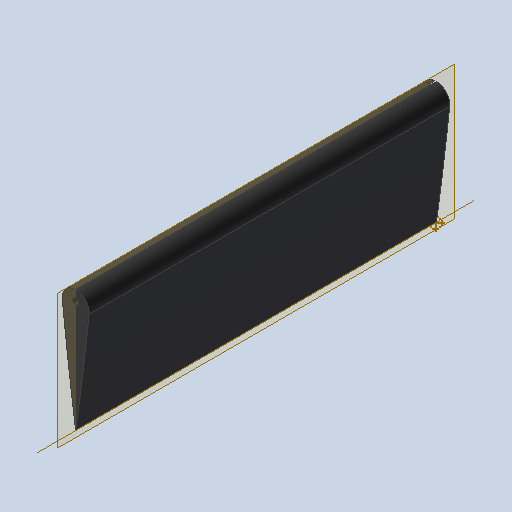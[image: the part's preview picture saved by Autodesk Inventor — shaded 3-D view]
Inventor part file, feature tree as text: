
AUTODESK INVENTOR PART (.ipt)
format: ipt  version: 2025.2 (Build 292293000, 293)  size: 150,016 bytes
history: native  units: in
note: dims shown in document units (in); Inventor stores cm internally (conversion verified against a paired STEP export)
features: other x5, sketch x1, plane x1
ambient origin geometry x8: Origin, YZ Plane, XZ Plane, XY Plane, X Axis, Y Axis, Z Axis, Center Point
bodies: Solid1 (feature_tree)
feature tree (7):
  other  "Elevator"
  other  "Solid1::Elevator"
  other  "TaggingFeature1"
  sketch  "Sketch3"  dims[d0=0.3937in]
  plane  "Work Plane1"
  other  "Work Axis1"
  other  "Work Point1"
